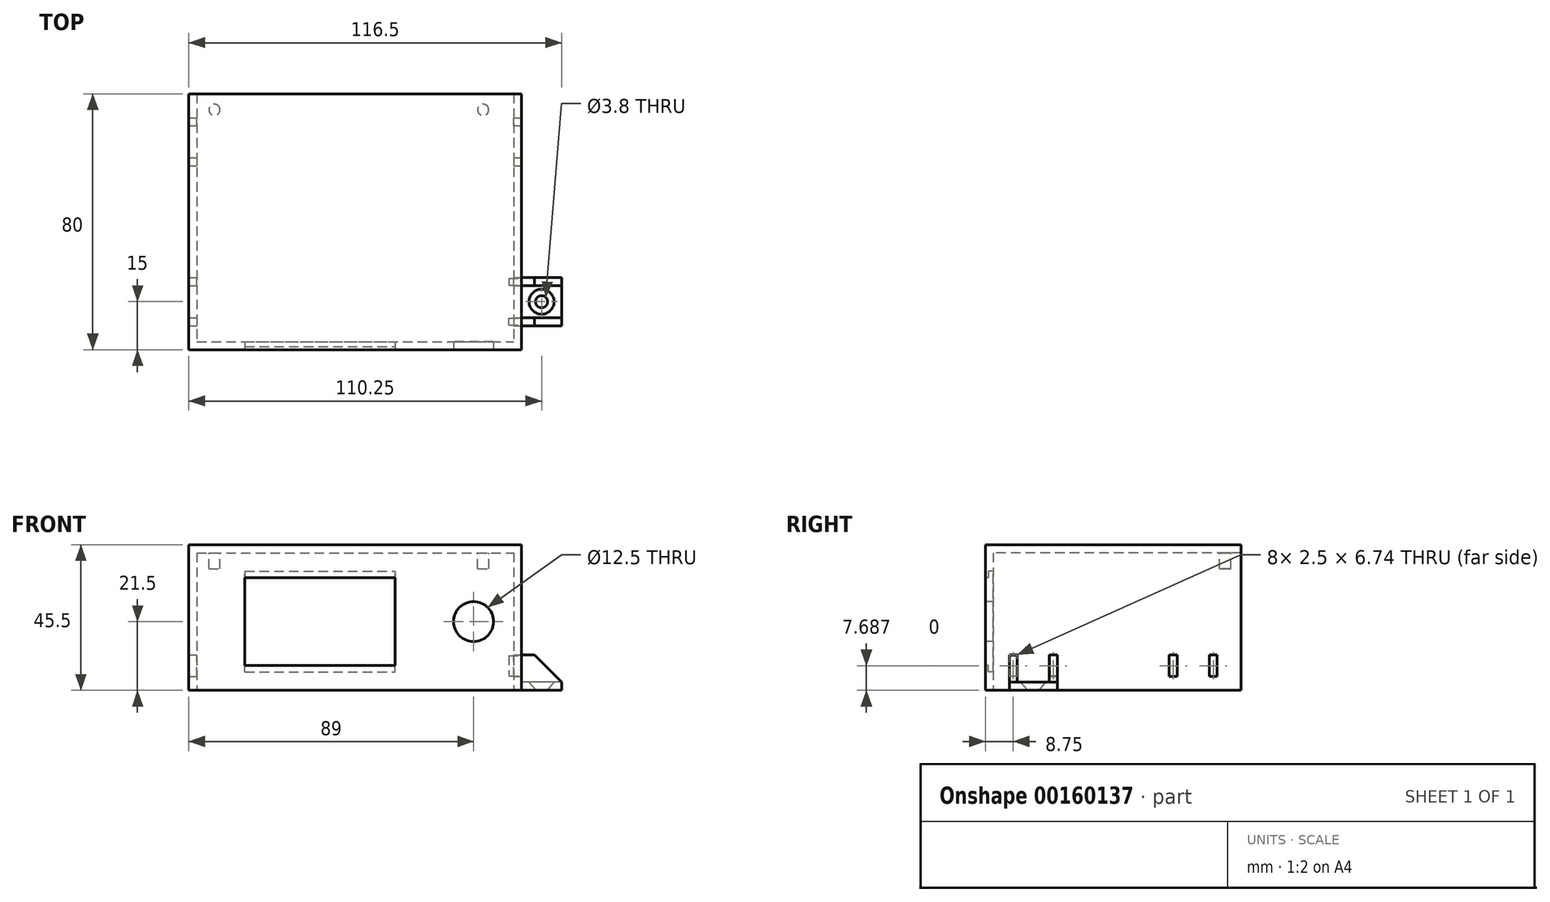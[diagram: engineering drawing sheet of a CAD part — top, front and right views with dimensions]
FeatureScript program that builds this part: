
annotation { "Feature Type Name" : "Feature", "Feature Type Description" : "" }
export const myFeature = defineFeature(function(context is Context, id is Id, definition is map)
    precondition{}
    {
        {
            assignVariable(context, id + "F0", {"name" : "shell_thickness", "anyValue" : 2.5});
        }
        {
            var Q0;
            Q0=qCreatedBy(makeId("Front.planeOp"),FACE);
            var sketch = newSketch(context, id + "F1", { "sketchPlane" : qUnion([Q0])});
            skLineSegment(sketch, "E0.bottom", {"start": v(0, 0) * mm, "end": v(47, 0) * mm});
            skLineSegment(sketch, "E0.top", {"start": v(0, 27.5) * mm, "end": v(47, 27.5) * mm});
            skLineSegment(sketch, "E0.left", {"start": v(0, 0) * mm, "end": v(0, 27.5) * mm});
            skLineSegment(sketch, "E0.right", {"start": v(47, 0) * mm, "end": v(47, 27.5) * mm});
            skLineSegment(sketch, "E1.bottom", {"start": v(-15, 35.25) * mm, "end": v(84, 35.25) * mm});
            skLineSegment(sketch, "E1.top", {"start": v(-17.5, -7.75) * mm, "end": v(86.5, -7.75) * mm});
            skLineSegment(sketch, "E1.left", {"start": v(-15, 35.25) * mm, "end": v(-15, -7.75) * mm});
            skLineSegment(sketch, "E1.right", {"start": v(84, 35.25) * mm, "end": v(84, -7.75) * mm});
            skPoint(sketch, "E2", {"position": v(47, 13.75) * mm});
            skPoint(sketch, "E3", {"position": v(84, 13.75) * mm});
            skLineSegment(sketch, "E4", {"start": v(-17.5, -7.75) * mm, "end": v(-17.5, 37.75) * mm});
            skLineSegment(sketch, "E5", {"start": v(-17.5, 37.75) * mm, "end": v(86.5, 37.75) * mm});
            skLineSegment(sketch, "E6", {"start": v(86.5, 37.75) * mm, "end": v(86.5, -7.75) * mm});
            skCircle(sketch, "E7", {"center": v(71.5, 13.75) * mm, "radius": 6.25 * mm});
            skPoint(sketch, "E8.endSnap0", {"position": v(91.5, -7.75) * mm});
            skSolve(sketch);
        }
        {
            var Q0;
            Q0=makeQuery(id+"F1.imprint","IMPRINT",FACE,{"disambiguationData":[TD([[makeQuery(id+"F1.imprint","IMPRINT",EDGE,{"derivedFrom":sQuery(id+"F1.wireOp",EDGE,"E1.bottom")}),1.0]])]});
            extrude(context, id + "F2", {"entities" : qUnion([Q0]), "oppositeDirection" : true, "depth" : 80 * mm});
        }
        {
            var Q0;
            Q0=makeQuery(id+"F1.imprint","IMPRINT",FACE,{"disambiguationData":[TD([[makeQuery(id+"F1.imprint","IMPRINT",EDGE,{"derivedFrom":sQuery(id+"F1.wireOp",EDGE,"E0.bottom")}),-1.0]])]});
            extrude(context, id + "F3", {"entities" : qUnion([Q0]), "operationType" : NewBodyOperationType.ADD, "oppositeDirection" : true, "depth" : 2.5 * mm});
        }
        {
            var Q0;
            Q0=makeQuery(id+"F2.opExtrude","SWEPT_FACE",FACE,{"disambiguationData":[OSD([sQuery(id+"F1.wireOp",EDGE,"E1.bottom")])]});
            var sketch = newSketch(context, id + "F4", { "sketchPlane" : qUnion([Q0])});
            skLineSegment(sketch, "E9", {"start": v(-9.5, 6.46) * mm, "end": v(-9.5, -86.26) * mm, "construction": true});
            skLineSegment(sketch, "E10", {"start": v(74.5, 5.28) * mm, "end": v(74.5, -90.64) * mm, "construction": true});
            skPoint(sketch, "E11", {"position": v(-9.5, -75) * mm});
            skPoint(sketch, "E12", {"position": v(74.5, -75) * mm});
            skCircle(sketch, "E13", {"center": v(-9.5, -75) * mm, "radius": 1.75 * mm});
            skCircle(sketch, "E14", {"center": v(74.5, -75) * mm, "radius": 1.75 * mm});
            skSolve(sketch);
        }
        {
            var Q0;
            Q0=makeQuery(id+"F4.imprint","IMPRINT",FACE,{"disambiguationData":[TD([[makeQuery(id+"F4.imprint","IMPRINT",EDGE,{"derivedFrom":sQuery(id+"F4.wireOp",EDGE,"E13")}),1.0]])]});
            var Q1;
            Q1=makeQuery(id+"F4.imprint","IMPRINT",FACE,{"disambiguationData":[TD([[makeQuery(id+"F4.imprint","IMPRINT",EDGE,{"derivedFrom":sQuery(id+"F4.wireOp",EDGE,"E14")}),1.0]])]});
            extrude(context, id + "F5", {"entities" : qUnion([Q0, Q1]), "operationType" : NewBodyOperationType.ADD, "depth" : 5 * mm});
        }
        {
            var Q0;
            Q0=makeQuery(id+"F2.opExtrude","SWEPT_FACE",FACE,{"disambiguationData":[OSD([sQuery(id+"F1.wireOp",EDGE,"E6")])]});
            var sketch = newSketch(context, id + "F6", { "sketchPlane" : qUnion([Q0])});
            skLineSegment(sketch, "E15", {"start": v(7.5, -7.75) * mm, "end": v(7.5, 7.25) * mm});
            skLineSegment(sketch, "E16", {"start": v(7.5, 7.25) * mm, "end": v(10, 7.25) * mm});
            skLineSegment(sketch, "E17", {"start": v(10, 7.25) * mm, "end": v(10, -5.25) * mm});
            skPoint(sketch, "E18", {"position": v(15, -7.75) * mm});
            skLineSegment(sketch, "E19", {"start": v(7.5, 3.3) * mm, "end": v(10, 3.3) * mm});
            skLineSegment(sketch, "E20", {"start": v(7.5, -3.43) * mm, "end": v(10, -3.43) * mm});
            skLineSegment(sketch, "E21", {"start": v(7.5, -7.75) * mm, "end": v(15, -7.75) * mm});
            skLineSegment(sketch, "E22", {"start": v(10, -5.25) * mm, "end": v(15, -5.25) * mm});
            skLineSegment(sketch, "E23", {"start": v(15, -7.75) * mm, "end": v(15, 7.25) * mm, "construction": true});
            skLineSegment(sketch, "E24.MirrorCS", {"start": v(20, 7.25) * mm, "end": v(20, -5.25) * mm});
            skLineSegment(sketch, "E25.MirrorCS", {"start": v(20, -5.25) * mm, "end": v(15, -5.25) * mm});
            skLineSegment(sketch, "E26.MirrorCS", {"start": v(22.5, -7.75) * mm, "end": v(15, -7.75) * mm});
            skLineSegment(sketch, "E27.MirrorCS", {"start": v(22.5, -7.75) * mm, "end": v(22.5, 7.25) * mm});
            skLineSegment(sketch, "E28.MirrorCS", {"start": v(22.5, 7.25) * mm, "end": v(20, 7.25) * mm});
            skLineSegment(sketch, "E29.MirrorCS", {"start": v(22.5, 3.3) * mm, "end": v(20, 3.3) * mm});
            skLineSegment(sketch, "E30.MirrorCS", {"start": v(22.5, -3.43) * mm, "end": v(20, -3.43) * mm});
            skLineSegment(sketch, "E31.0", {"start": v(80, 37.75) * mm, "end": v(0, 37.75) * mm, "construction": true});
            skLineSegment(sketch, "E32.0", {"start": v(80, -7.75) * mm, "end": v(0, -7.75) * mm, "construction": true});
            skLineSegment(sketch, "E33", {"start": v(40, 37.75) * mm, "end": v(40, -7.75) * mm, "construction": true});
            skLineSegment(sketch, "E34.MirrorCS", {"start": v(57.5, -7.75) * mm, "end": v(57.5, 7.25) * mm});
            skLineSegment(sketch, "E35.MirrorCS", {"start": v(60, 7.25) * mm, "end": v(60, -5.25) * mm});
            skLineSegment(sketch, "E36.MirrorCS", {"start": v(70, 7.25) * mm, "end": v(70, -5.25) * mm});
            skLineSegment(sketch, "E37.MirrorCS", {"start": v(72.5, -7.75) * mm, "end": v(72.5, 7.25) * mm});
            skLineSegment(sketch, "E38.MirrorCS", {"start": v(72.5, 3.3) * mm, "end": v(70, 3.3) * mm});
            skLineSegment(sketch, "E39.MirrorCS", {"start": v(72.5, -3.43) * mm, "end": v(70, -3.43) * mm});
            skLineSegment(sketch, "E40.MirrorCS", {"start": v(57.5, -3.43) * mm, "end": v(60, -3.43) * mm});
            skLineSegment(sketch, "E41.MirrorCS", {"start": v(57.5, 3.3) * mm, "end": v(60, 3.3) * mm});
            skLineSegment(sketch, "E42.MirrorCS", {"start": v(60, -5.25) * mm, "end": v(65, -5.25) * mm});
            skLineSegment(sketch, "E43.MirrorCS", {"start": v(70, -5.25) * mm, "end": v(65, -5.25) * mm});
            skLineSegment(sketch, "E44.MirrorCS", {"start": v(0, -7.75) * mm, "end": v(80, -7.75) * mm, "construction": true});
            skLineSegment(sketch, "E45.MirrorCS", {"start": v(72.5, 7.25) * mm, "end": v(70, 7.25) * mm});
            skLineSegment(sketch, "E46.MirrorCS", {"start": v(57.5, 7.25) * mm, "end": v(60, 7.25) * mm});
            skLineSegment(sketch, "E47.bottom", {"start": v(7.7, 3.1) * mm, "end": v(9.8, 3.1) * mm});
            skLineSegment(sketch, "E47.top", {"start": v(7.7, -3.23) * mm, "end": v(9.8, -3.23) * mm});
            skLineSegment(sketch, "E47.left", {"start": v(7.7, 3.1) * mm, "end": v(7.7, -3.23) * mm});
            skLineSegment(sketch, "E47.right", {"start": v(9.8, 3.1) * mm, "end": v(9.8, -3.23) * mm});
            skLineSegment(sketch, "E48.MirrorCS", {"start": v(22.3, 3.1) * mm, "end": v(20.2, 3.1) * mm});
            skLineSegment(sketch, "E49.MirrorCS", {"start": v(22.3, 3.1) * mm, "end": v(22.3, -3.23) * mm});
            skLineSegment(sketch, "E50.MirrorCS", {"start": v(22.3, -3.23) * mm, "end": v(20.2, -3.23) * mm});
            skLineSegment(sketch, "E51.MirrorCS", {"start": v(20.2, 3.1) * mm, "end": v(20.2, -3.23) * mm});
            skSolve(sketch);
        }
        {
            var Q0;
            {var subQ0=sQuery(id+"F6.wireOp",EDGE,"E19");Q0=makeQuery(id+"F6.imprint","IMPRINT",FACE,{"disambiguationData":[TD([[makeQuery(id+"F6.imprint","IMPRINT",EDGE,{"derivedFrom":subQ0}),-1.0]])]});}
            var Q1;
            {var subQ0=sQuery(id+"F6.wireOp",EDGE,"E29.MirrorCS");Q1=makeQuery(id+"F6.imprint","IMPRINT",FACE,{"disambiguationData":[TD([[makeQuery(id+"F6.imprint","IMPRINT",EDGE,{"derivedFrom":subQ0}),1.0]])]});}
            var Q2;
            {var subQ0=sQuery(id+"F6.wireOp",EDGE,"E40.MirrorCS");Q2=makeQuery(id+"F6.imprint","IMPRINT",FACE,{"disambiguationData":[TD([[makeQuery(id+"F6.imprint","IMPRINT",EDGE,{"derivedFrom":subQ0}),1.0]])]});}
            var Q3;
            {var subQ0=sQuery(id+"F6.wireOp",EDGE,"E38.MirrorCS");Q3=makeQuery(id+"F6.imprint","IMPRINT",FACE,{"disambiguationData":[TD([[makeQuery(id+"F6.imprint","IMPRINT",EDGE,{"derivedFrom":subQ0}),1.0]])]});}
            var Q4;
            Q4=makeQuery(id+"F6.imprint","IMPRINT",FACE,{"disambiguationData":[TD([[makeQuery(id+"F6.imprint","IMPRINT",EDGE,{"derivedFrom":sQuery(id+"F6.wireOp",EDGE,"E47.bottom")}),-1.0]])]});
            var Q5;
            Q5=makeQuery(id+"F6.imprint","IMPRINT",FACE,{"disambiguationData":[TD([[makeQuery(id+"F6.imprint","IMPRINT",EDGE,{"derivedFrom":sQuery(id+"F6.wireOp",EDGE,"E48.MirrorCS")}),1.0]])]});
            var Q6;
            Q6=makeQuery(id+"F2.opExtrude","SWEPT_FACE",FACE,{"disambiguationData":[OSD([sQuery(id+"F1.wireOp",EDGE,"E4")])]});
            extrude(context, id + "F7", {"entities" : qUnion([Q0, Q1, Q2, Q3, Q4, Q5]), "operationType" : NewBodyOperationType.REMOVE, "endBound" : BoundingType.UP_TO_SURFACE, "oppositeDirection" : true, "endBoundEntityFace" : qUnion([Q6]), "depth" : 25 * mm});
        }
        {
            var Q0;
            {var subQ0=sQuery(id+"F6.wireOp",EDGE,"E19");Q0=makeQuery(id+"F6.imprint","IMPRINT",FACE,{"disambiguationData":[TD([[makeQuery(id+"F6.imprint","IMPRINT",EDGE,{"derivedFrom":subQ0}),-1.0]])]});}
            var Q1;
            {var subQ5=sQuery(id+"F6.wireOp",EDGE,"E20");Q1=makeQuery(id+"F6.imprint","IMPRINT",FACE,{"disambiguationData":[TD([[makeQuery(id+"F6.imprint","IMPRINT",EDGE,{"derivedFrom":subQ5}),-1.0]])]});}
            var Q2;
            {var subQ0=sQuery(id+"F6.wireOp",EDGE,"E29.MirrorCS");Q2=makeQuery(id+"F6.imprint","IMPRINT",FACE,{"disambiguationData":[TD([[makeQuery(id+"F6.imprint","IMPRINT",EDGE,{"derivedFrom":subQ0}),1.0]])]});}
            var Q3;
            Q3=makeQuery(id+"F6.imprint","IMPRINT",FACE,{"disambiguationData":[TD([[makeQuery(id+"F6.imprint","IMPRINT",EDGE,{"derivedFrom":sQuery(id+"F6.wireOp",EDGE,"E47.bottom")}),-1.0]])]});
            var Q4;
            Q4=makeQuery(id+"F6.imprint","IMPRINT",FACE,{"disambiguationData":[TD([[makeQuery(id+"F6.imprint","IMPRINT",EDGE,{"derivedFrom":sQuery(id+"F6.wireOp",EDGE,"E48.MirrorCS")}),1.0]])]});
            extrude(context, id + "F8", {"entities" : qUnion([Q0, Q1, Q2, Q3, Q4]), "depth" : 12.5 * mm});
        }
        {
            var Q0;
            Q0=makeQuery(id+"F6.imprint","IMPRINT",FACE,{"disambiguationData":[TD([[makeQuery(id+"F6.imprint","IMPRINT",EDGE,{"derivedFrom":sQuery(id+"F6.wireOp",EDGE,"E47.bottom")}),-1.0]])]});
            var Q1;
            Q1=makeQuery(id+"F6.imprint","IMPRINT",FACE,{"disambiguationData":[TD([[makeQuery(id+"F6.imprint","IMPRINT",EDGE,{"derivedFrom":sQuery(id+"F6.wireOp",EDGE,"E48.MirrorCS")}),1.0]])]});
            var Q2;
            Q2=makeQuery(id+"F2.opExtrude","SWEPT_FACE",FACE,{"disambiguationData":[OSD([sQuery(id+"F1.wireOp",EDGE,"E1.right")])]});
            var Q3;
            Q3=makeQuery(id+"F2.opExtrude","SWEPT_BODY",BODY,{"disambiguationData":[OSD([sQuery(id+"F1.wireOp",EDGE,"E1.bottom"),sQuery(id+"F1.wireOp",EDGE,"E1.top"),sQuery(id+"F1.wireOp",EDGE,"E1.left"),sQuery(id+"F1.wireOp",EDGE,"E1.right"),sQuery(id+"F1.wireOp",EDGE,"E4"),sQuery(id+"F1.wireOp",EDGE,"E5"),sQuery(id+"F1.wireOp",EDGE,"E6")])]});
            extrude(context, id + "F9", {"entities" : qUnion([Q0, Q1]), "operationType" : NewBodyOperationType.ADD, "oppositeDirection" : true, "endBoundEntityFace" : qUnion([Q2]), "endBoundEntityBody" : qUnion([Q3]), "depth" : (1.5 + (getVariable(context, 'shell_thickness'))) * mm});
        }
        {
            var Q0;
            Q0=makeQuery(id+"F8.opExtrude","CAP_EDGE",EDGE,{"disambiguationData":[OSD([sQuery(id+"F6.wireOp",EDGE,"E16")])],"isStart":false});
            var Q1;
            Q1=makeQuery(id+"F8.opExtrude","CAP_EDGE",EDGE,{"disambiguationData":[OSD([sQuery(id+"F6.wireOp",EDGE,"E28.MirrorCS")])],"isStart":false});
            var Q2;
            Q2=makeQuery(id+"F8.opExtrude","CAP_EDGE",EDGE,{"disambiguationData":[OSD([sQuery(id+"F6.wireOp",EDGE,"E19")])],"isStart":false});
            var Q3;
            Q3=makeQuery(id+"F8.opExtrude","CAP_EDGE",EDGE,{"disambiguationData":[OSD([sQuery(id+"F6.wireOp",EDGE,"E29.MirrorCS")])],"isStart":false});
            chamfer(context, id + "F10", {"entities" : qUnion([Q0, Q1, Q2, Q3]), "width" : 8.5 * mm, "tangentPropagation" : true});
        }
        {
            var Q0;
            Q0=makeQuery(id+"F8.opExtrude","SWEPT_FACE",FACE,{"disambiguationData":[OSD([sQuery(id+"F6.wireOp",EDGE,"E22"),sQuery(id+"F6.wireOp",EDGE,"E25.MirrorCS")])]});
            var sketch = newSketch(context, id + "F11", { "sketchPlane" : qUnion([Q0])});
            skPoint(sketch, "E52", {"position": v(92.75, 15) * mm});
            skPoint(sketch, "E52.positionSnap0", {"position": v(86.5, 15) * mm});
            skSolve(sketch);
        }
        {
            var Q0;
            Q0=sQuery(id+"F11.wireOp",VERTEX,"E52");
            var Q1;
            Q1=makeQuery(id+"F8.opExtrude","SWEPT_BODY",BODY,{"disambiguationData":[OSD([sQuery(id+"F6.wireOp",EDGE,"E15"),sQuery(id+"F6.wireOp",EDGE,"E16"),sQuery(id+"F6.wireOp",EDGE,"E17"),sQuery(id+"F6.wireOp",EDGE,"E21"),sQuery(id+"F6.wireOp",EDGE,"E22"),sQuery(id+"F6.wireOp",EDGE,"E24.MirrorCS"),sQuery(id+"F6.wireOp",EDGE,"E25.MirrorCS"),sQuery(id+"F6.wireOp",EDGE,"E26.MirrorCS"),sQuery(id+"F6.wireOp",EDGE,"E27.MirrorCS"),sQuery(id+"F6.wireOp",EDGE,"E28.MirrorCS")])]});
            hole(context, id + "F12", {"style" : HoleStyle.C_SINK, "endStyle" : HoleEndStyle.THROUGH, "standardTappedOrClearance" : lookupTablePath({ "standard" : "ANSI", "fit" : "Normal (ASME)", "size" : "#6", "type" : "Clearance" }), "standardBlindInLast" : lookupTablePath({ "fit" : "Free", "standard" : "ANSI", "size" : "#6", "type" : "Clearance" }), "holeDiameter" : 3.8 * mm, "cSinkDiameter" : 7.8 * mm, "cSinkAngle" : 82 * degree, "locations" : qUnion([Q0]), "scope" : qUnion([Q1]), "isTappedThrough" : true});
        }
        {
            var Q0;
            Q0=makeQuery(id+"F3.opExtrude","SWEPT_FACE",FACE,{"disambiguationData":[OSD([sQuery(id+"F1.wireOp",EDGE,"E0.bottom")])]});
            var sketch = newSketch(context, id + "F13", { "sketchPlane" : qUnion([Q0])});
            skLineSegment(sketch, "E53.0", {"start": v(0, 2.5) * mm, "end": v(47, 2.5) * mm});
            skLineSegment(sketch, "E54", {"start": v(0, 1) * mm, "end": v(47, 1) * mm});
            skLineSegment(sketch, "E55", {"start": v(47, 1.25) * mm, "end": v(47, 2.5) * mm});
            skLineSegment(sketch, "E56", {"start": v(0, 2.5) * mm, "end": v(0, 1) * mm});
            skSolve(sketch);
        }
        {
            var Q0;
            Q0=makeQuery(id+"F13.imprint","IMPRINT",FACE,{"disambiguationData":[TD([[makeQuery(id+"F13.imprint","IMPRINT",EDGE,{"derivedFrom":sQuery(id+"F13.wireOp",EDGE,"E53.0")}),-1.0]])]});
            extrude(context, id + "F14", {"entities" : qUnion([Q0]), "operationType" : NewBodyOperationType.REMOVE, "oppositeDirection" : true, "depth" : 2 * mm});
        }
        {
            var Q0;
            Q0=makeQuery(id+"F3.opExtrude","SWEPT_FACE",FACE,{"disambiguationData":[OSD([sQuery(id+"F1.wireOp",EDGE,"E0.top")])]});
            var sketch = newSketch(context, id + "F15", { "sketchPlane" : qUnion([Q0])});
            skLineSegment(sketch, "E57.0", {"start": v(0, -1) * mm, "end": v(47, -1) * mm});
            skLineSegment(sketch, "E58.0", {"start": v(0, -2.5) * mm, "end": v(47, -2.5) * mm});
            skLineSegment(sketch, "E59", {"start": v(0, -1) * mm, "end": v(0, -2.5) * mm});
            skLineSegment(sketch, "E60", {"start": v(47, -2.5) * mm, "end": v(47, -1) * mm});
            skSolve(sketch);
        }
        {
            var Q0;
            Q0=makeQuery(id+"F15.imprint","IMPRINT",FACE,{"disambiguationData":[TD([[makeQuery(id+"F15.imprint","IMPRINT",EDGE,{"derivedFrom":sQuery(id+"F15.wireOp",EDGE,"E57.0")}),-1.0]])]});
            extrude(context, id + "F16", {"entities" : qUnion([Q0]), "operationType" : NewBodyOperationType.REMOVE, "oppositeDirection" : true, "depth" : 2 * mm});
        }
    });
